# Revit family: 317_48b06837791741a087193c4d1e406d
name_source: partatom
category: Mechanical Equipment
units: mm (PartAtom-declared; Revit-internal decimal feet)

## family parameters
Always vertical = Yes
Cut with Voids When Loaded = No
Part Type = Normal
Room Calculation Point = No
Round Connector Dimension = Use Diameter
Shared = No
Work Plane-Based = No

## types (1)
- FSK101 40-W
    BH = 800 mm  [stored 2.62467 ft]
    BH2 = 400 mm  [stored 1.31234 ft]
    BL2 = 300 mm  [stored 0.984252 ft]
    BL4 = 120 mm
    BL41 = 240 mm
    BW = 300 mm  [stored 0.984252 ft]
    BW4 = 75 mm  [stored 0.246063 ft]
    Description = Fresh hydro unit FSK101 40 l - Wilo
    MC Product Code = FSK101 40-W
    Manufacturer = ESBE
    PPR = 25 mm
    PPS = 25 mm
    PSR = 25 mm
    PSS = 25 mm
    QmdConnectorList = 321;PPS;322;PSS;351;PPR;352;PSR
    URL = http://www.esbe.eu
    W1 = 32 mm  [stored 0.104987 ft]
    W11 = 223 mm
    W11__ve = -223 mm  [stored -0.731627 ft]
    X = 100 mm  [stored 0.328084 ft]
    magiPartTypeId = 317
    magiProductFamilyId = 48b06837791741a087193c4d1e406d
    magiProductId = 48b06837791741a087193c4d1e406d

note: [stored X ft] marks values corroborated as IEEE doubles in the binary element streams (Revit-internal decimal feet)

## geometry (parser evidence)
native form markers: Sweep x2
no freeform markers — native parametric forms only
